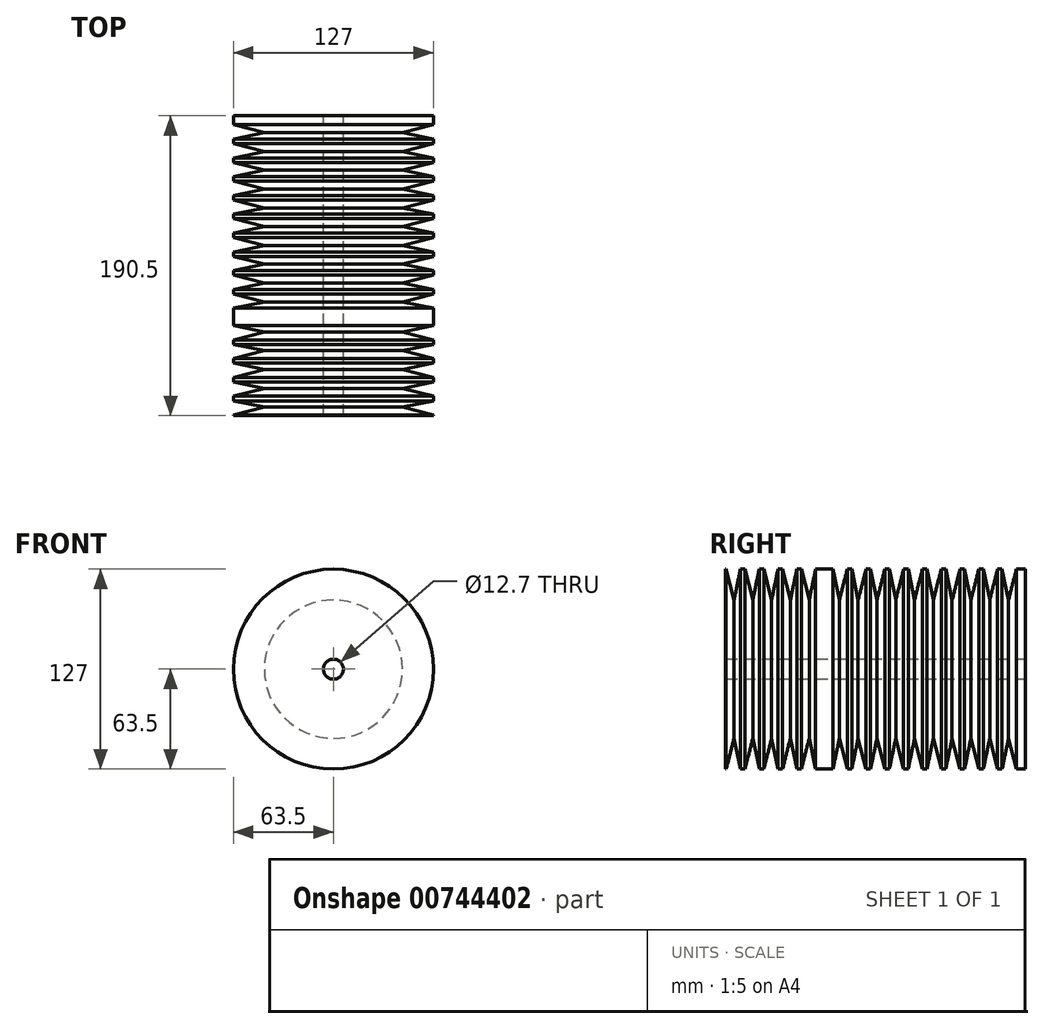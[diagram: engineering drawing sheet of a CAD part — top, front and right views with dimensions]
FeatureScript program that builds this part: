
annotation { "Feature Type Name" : "Feature", "Feature Type Description" : "" }
export const myFeature = defineFeature(function(context is Context, id is Id, definition is map)
    precondition{}
    {
        {
            var Q0;
            Q0=qCreatedBy(makeId("Front.planeOp"),FACE);
            var sketch = newSketch(context, id + "F0", { "sketchPlane" : qUnion([Q0])});
            skCircle(sketch, "E0", {"center": v(0, 0) * mm, "radius": 63.5 * mm});
            skCircle(sketch, "E1", {"center": v(0, 0) * mm, "radius": 6.35 * mm});
            skSolve(sketch);
        }
        {
            var Q0;
            Q0=makeQuery(id+"F0.imprint","IMPRINT",FACE,{"disambiguationData":[TD([[makeQuery(id+"F0.imprint","IMPRINT",EDGE,{"derivedFrom":sQuery(id+"F0.wireOp",EDGE,"E0")}),1.0]])]});
            extrude(context, id + "F1", {"entities" : qUnion([Q0]), "depth" : 127 * mm});
        }
        {
            var Q0;
            Q0=qCreatedBy(makeId("Right.planeOp"),FACE);
            var sketch = newSketch(context, id + "F2", { "sketchPlane" : qUnion([Q0])});
            skLineSegment(sketch, "E2", {"start": v(0, 64.94) * mm, "end": v(-127.74, 64.94) * mm});
            skLineSegment(sketch, "E3", {"start": v(-5.36, 64.94) * mm, "end": v(-10.73, 43.9) * mm});
            skLineSegment(sketch, "E4", {"start": v(-10.73, 43.9) * mm, "end": v(-15.08, 64.94) * mm});
            skLineSegment(sketch, "E5.1.0.0", {"start": v(-17.3, 64.94) * mm, "end": v(-22.67, 43.9) * mm});
            skLineSegment(sketch, "E5.1.0.1", {"start": v(-22.67, 43.9) * mm, "end": v(-27.02, 64.94) * mm});
            skLineSegment(sketch, "E5.1.0.2", {"start": v(-11.94, 64.94) * mm, "end": v(-139.68, 64.94) * mm});
            skLineSegment(sketch, "E5.2.0.0", {"start": v(-29.24, 64.94) * mm, "end": v(-34.6, 43.9) * mm});
            skLineSegment(sketch, "E5.2.0.1", {"start": v(-34.6, 43.9) * mm, "end": v(-38.95, 64.94) * mm});
            skLineSegment(sketch, "E5.2.0.2", {"start": v(-23.88, 64.94) * mm, "end": v(-151.62, 64.94) * mm});
            skLineSegment(sketch, "E5.3.0.0", {"start": v(-41.17, 64.94) * mm, "end": v(-46.54, 43.9) * mm});
            skLineSegment(sketch, "E5.3.0.1", {"start": v(-46.54, 43.9) * mm, "end": v(-50.9, 64.94) * mm});
            skLineSegment(sketch, "E5.3.0.2", {"start": v(-35.81, 64.94) * mm, "end": v(-163.56, 64.94) * mm});
            skLineSegment(sketch, "E5.4.0.0", {"start": v(-53.11, 64.94) * mm, "end": v(-58.48, 43.9) * mm});
            skLineSegment(sketch, "E5.4.0.1", {"start": v(-58.48, 43.9) * mm, "end": v(-62.83, 64.94) * mm});
            skLineSegment(sketch, "E5.4.0.2", {"start": v(-47.75, 64.94) * mm, "end": v(-175.5, 64.94) * mm});
            skLineSegment(sketch, "E5.5.0.0", {"start": v(-65.05, 64.94) * mm, "end": v(-70.42, 43.9) * mm});
            skLineSegment(sketch, "E5.5.0.1", {"start": v(-70.42, 43.9) * mm, "end": v(-74.77, 64.94) * mm});
            skLineSegment(sketch, "E5.5.0.2", {"start": v(-59.7, 64.94) * mm, "end": v(-187.43, 64.94) * mm});
            skLineSegment(sketch, "E5.6.0.0", {"start": v(-76.99, 64.94) * mm, "end": v(-82.36, 43.9) * mm});
            skLineSegment(sketch, "E5.6.0.1", {"start": v(-82.36, 43.9) * mm, "end": v(-86.7, 64.94) * mm});
            skLineSegment(sketch, "E5.6.0.2", {"start": v(-71.63, 64.94) * mm, "end": v(-199.37, 64.94) * mm});
            skLineSegment(sketch, "E5.7.0.0", {"start": v(-88.93, 64.94) * mm, "end": v(-94.3, 43.9) * mm});
            skLineSegment(sketch, "E5.7.0.1", {"start": v(-94.3, 43.9) * mm, "end": v(-98.64, 64.94) * mm});
            skLineSegment(sketch, "E5.7.0.2", {"start": v(-83.57, 64.94) * mm, "end": v(-211.31, 64.94) * mm});
            skLineSegment(sketch, "E5.8.0.0", {"start": v(-100.86, 64.94) * mm, "end": v(-106.23, 43.9) * mm});
            skLineSegment(sketch, "E5.8.0.1", {"start": v(-106.23, 43.9) * mm, "end": v(-110.58, 64.94) * mm});
            skLineSegment(sketch, "E5.8.0.2", {"start": v(-95.5, 64.94) * mm, "end": v(-223.25, 64.94) * mm});
            skLineSegment(sketch, "E5.9.0.0", {"start": v(-112.8, 64.94) * mm, "end": v(-118.17, 43.9) * mm});
            skLineSegment(sketch, "E5.9.0.1", {"start": v(-118.17, 43.9) * mm, "end": v(-122.52, 64.94) * mm});
            skLineSegment(sketch, "E5.9.0.2", {"start": v(-107.44, 64.94) * mm, "end": v(-235.19, 64.94) * mm});
            skLineSegment(sketch, "E5.direction1", {"start": v(-10.73, 43.9) * mm, "end": v(-22.67, 43.9) * mm, "construction": true});
            skLineSegment(sketch, "E6", {"start": v(-127.74, 64.94) * mm, "end": v(-127.74, -5.8) * mm, "construction": true});
            skLineSegment(sketch, "E7.MirrorCS", {"start": v(-137.32, 43.9) * mm, "end": v(-132.97, 64.94) * mm});
            skLineSegment(sketch, "E8.MirrorCS", {"start": v(-142.69, 64.94) * mm, "end": v(-137.32, 43.9) * mm});
            skLineSegment(sketch, "E9.MirrorCS", {"start": v(-149.26, 43.9) * mm, "end": v(-144.9, 64.94) * mm});
            skLineSegment(sketch, "E10.MirrorCS", {"start": v(-154.63, 64.94) * mm, "end": v(-149.26, 43.9) * mm});
            skLineSegment(sketch, "E11.MirrorCS", {"start": v(-161.2, 43.9) * mm, "end": v(-156.85, 64.94) * mm});
            skLineSegment(sketch, "E12.MirrorCS", {"start": v(-166.56, 64.94) * mm, "end": v(-161.2, 43.9) * mm});
            skLineSegment(sketch, "E13.MirrorCS", {"start": v(-173.13, 43.9) * mm, "end": v(-168.78, 64.94) * mm});
            skLineSegment(sketch, "E14.MirrorCS", {"start": v(-178.5, 64.94) * mm, "end": v(-173.13, 43.9) * mm});
            skLineSegment(sketch, "E15.MirrorCS", {"start": v(-185.07, 43.9) * mm, "end": v(-180.72, 64.94) * mm});
            skLineSegment(sketch, "E16.MirrorCS", {"start": v(-190.44, 64.94) * mm, "end": v(-185.07, 43.9) * mm});
            skLineSegment(sketch, "E17.MirrorCS", {"start": v(-197, 43.9) * mm, "end": v(-192.66, 64.94) * mm});
            skLineSegment(sketch, "E18.MirrorCS", {"start": v(-202.38, 64.94) * mm, "end": v(-197, 43.9) * mm});
            skLineSegment(sketch, "E19.MirrorCS", {"start": v(-208.95, 43.9) * mm, "end": v(-204.6, 64.94) * mm});
            skLineSegment(sketch, "E20.MirrorCS", {"start": v(-214.32, 64.94) * mm, "end": v(-208.95, 43.9) * mm});
            skLineSegment(sketch, "E21.MirrorCS", {"start": v(-220.88, 43.9) * mm, "end": v(-216.54, 64.94) * mm});
            skLineSegment(sketch, "E22.MirrorCS", {"start": v(-226.25, 64.94) * mm, "end": v(-220.88, 43.9) * mm});
            skLineSegment(sketch, "E23.MirrorCS", {"start": v(-232.82, 43.9) * mm, "end": v(-228.47, 64.94) * mm});
            skLineSegment(sketch, "E24.MirrorCS", {"start": v(-238.2, 64.94) * mm, "end": v(-232.82, 43.9) * mm});
            skLineSegment(sketch, "E25.MirrorCS", {"start": v(-244.76, 43.9) * mm, "end": v(-240.41, 64.94) * mm});
            skSolve(sketch);
        }
        {
            var Q0;
            {var subQ3=sQuery(id+"F2.wireOp",EDGE,"E3");Q0=makeQuery(id+"F2.imprint","IMPRINT",FACE,{"disambiguationData":[TD([[makeQuery(id+"F2.imprint","IMPRINT",EDGE,{"derivedFrom":subQ3}),-1.0]])]});}
            var Q1;
            {var subQ0=sQuery(id+"F2.wireOp",EDGE,"E5.1.0.0");Q1=makeQuery(id+"F2.imprint","IMPRINT",FACE,{"disambiguationData":[TD([[makeQuery(id+"F2.imprint","IMPRINT",EDGE,{"derivedFrom":subQ0}),-1.0]])]});}
            var Q2;
            {var subQ0=sQuery(id+"F2.wireOp",EDGE,"E5.2.0.0");Q2=makeQuery(id+"F2.imprint","IMPRINT",FACE,{"disambiguationData":[TD([[makeQuery(id+"F2.imprint","IMPRINT",EDGE,{"derivedFrom":subQ0}),-1.0]])]});}
            var Q3;
            {var subQ0=sQuery(id+"F2.wireOp",EDGE,"E5.3.0.0");Q3=makeQuery(id+"F2.imprint","IMPRINT",FACE,{"disambiguationData":[TD([[makeQuery(id+"F2.imprint","IMPRINT",EDGE,{"derivedFrom":subQ0}),-1.0]])]});}
            var Q4;
            {var subQ0=sQuery(id+"F2.wireOp",EDGE,"E5.4.0.0");Q4=makeQuery(id+"F2.imprint","IMPRINT",FACE,{"disambiguationData":[TD([[makeQuery(id+"F2.imprint","IMPRINT",EDGE,{"derivedFrom":subQ0}),-1.0]])]});}
            var Q5;
            {var subQ0=sQuery(id+"F2.wireOp",EDGE,"E5.5.0.0");Q5=makeQuery(id+"F2.imprint","IMPRINT",FACE,{"disambiguationData":[TD([[makeQuery(id+"F2.imprint","IMPRINT",EDGE,{"derivedFrom":subQ0}),-1.0]])]});}
            var Q6;
            {var subQ0=sQuery(id+"F2.wireOp",EDGE,"E5.6.0.0");Q6=makeQuery(id+"F2.imprint","IMPRINT",FACE,{"disambiguationData":[TD([[makeQuery(id+"F2.imprint","IMPRINT",EDGE,{"derivedFrom":subQ0}),-1.0]])]});}
            var Q7;
            {var subQ0=sQuery(id+"F2.wireOp",EDGE,"E5.7.0.0");Q7=makeQuery(id+"F2.imprint","IMPRINT",FACE,{"disambiguationData":[TD([[makeQuery(id+"F2.imprint","IMPRINT",EDGE,{"derivedFrom":subQ0}),-1.0]])]});}
            var Q8;
            {var subQ0=sQuery(id+"F2.wireOp",EDGE,"E5.8.0.0");Q8=makeQuery(id+"F2.imprint","IMPRINT",FACE,{"disambiguationData":[TD([[makeQuery(id+"F2.imprint","IMPRINT",EDGE,{"derivedFrom":subQ0}),-1.0]])]});}
            var Q9;
            {var subQ0=sQuery(id+"F2.wireOp",EDGE,"E5.9.0.0");Q9=makeQuery(id+"F2.imprint","IMPRINT",FACE,{"disambiguationData":[TD([[makeQuery(id+"F2.imprint","IMPRINT",EDGE,{"derivedFrom":subQ0}),-1.0]])]});}
            var Q10;
            {var subQ0=sQuery(id+"F2.wireOp",EDGE,"E7.MirrorCS");Q10=makeQuery(id+"F2.imprint","IMPRINT",FACE,{"disambiguationData":[TD([[makeQuery(id+"F2.imprint","IMPRINT",EDGE,{"derivedFrom":subQ0}),1.0]])]});}
            var Q11;
            {var subQ0=sQuery(id+"F2.wireOp",EDGE,"E9.MirrorCS");Q11=makeQuery(id+"F2.imprint","IMPRINT",FACE,{"disambiguationData":[TD([[makeQuery(id+"F2.imprint","IMPRINT",EDGE,{"derivedFrom":subQ0}),1.0]])]});}
            var Q12;
            {var subQ0=sQuery(id+"F2.wireOp",EDGE,"E11.MirrorCS");Q12=makeQuery(id+"F2.imprint","IMPRINT",FACE,{"disambiguationData":[TD([[makeQuery(id+"F2.imprint","IMPRINT",EDGE,{"derivedFrom":subQ0}),1.0]])]});}
            var Q13;
            {var subQ0=sQuery(id+"F2.wireOp",EDGE,"E13.MirrorCS");Q13=makeQuery(id+"F2.imprint","IMPRINT",FACE,{"disambiguationData":[TD([[makeQuery(id+"F2.imprint","IMPRINT",EDGE,{"derivedFrom":subQ0}),1.0]])]});}
            var Q14;
            {var subQ0=sQuery(id+"F2.wireOp",EDGE,"E15.MirrorCS");Q14=makeQuery(id+"F2.imprint","IMPRINT",FACE,{"disambiguationData":[TD([[makeQuery(id+"F2.imprint","IMPRINT",EDGE,{"derivedFrom":subQ0}),1.0]])]});}
            var Q15;
            {var subQ0=sQuery(id+"F2.wireOp",EDGE,"E17.MirrorCS");Q15=makeQuery(id+"F2.imprint","IMPRINT",FACE,{"disambiguationData":[TD([[makeQuery(id+"F2.imprint","IMPRINT",EDGE,{"derivedFrom":subQ0}),1.0]])]});}
            var Q16;
            Q16=makeQuery(id+"F1.opExtrude","CAP_EDGE",EDGE,{"disambiguationData":[OSD([sQuery(id+"F0.wireOp",EDGE,"E0")])],"isStart":false});
            revolve(context, id + "F3", {"operationType" : NewBodyOperationType.REMOVE, "entities" : qUnion([Q0, Q1, Q2, Q3, Q4, Q5, Q6, Q7, Q8, Q9, Q10, Q11, Q12, Q13, Q14, Q15]), "axis" : qUnion([Q16]), "revolveType" : RevolveType.FULL, "oppositeDirection" : true});
        }
        {
            var Q0;
            Q0=makeQuery(id+"F1.opExtrude","CAP_FACE",FACE,{"disambiguationData":[OSD([sQuery(id+"F0.wireOp",EDGE,"E0"),sQuery(id+"F0.wireOp",EDGE,"E1")])],"isStart":false});
            extrude(context, id + "F4", {"entities" : qUnion([Q0]), "operationType" : NewBodyOperationType.ADD, "depth" : 63.5 * mm});
        }
        {
            var Q0;
            {var subQ0=sQuery(id+"F2.wireOp",EDGE,"E7.MirrorCS");Q0=makeQuery(id+"F2.imprint","IMPRINT",FACE,{"disambiguationData":[TD([[makeQuery(id+"F2.imprint","IMPRINT",EDGE,{"derivedFrom":subQ0}),1.0]])]});}
            var Q1;
            Q1=qSketchRegion(id+"F2",true);
            var Q2;
            Q2=makeQuery(id+"F4.opExtrude","CAP_EDGE",EDGE,{"disambiguationData":[OSD([sQuery(id+"F0.wireOp",EDGE,"E0")])],"isStart":false});
            revolve(context, id + "F5", {"operationType" : NewBodyOperationType.REMOVE, "entities" : qUnion([Q0, Q1]), "axis" : qUnion([Q2]), "revolveType" : RevolveType.FULL, "oppositeDirection" : true});
        }
    });
